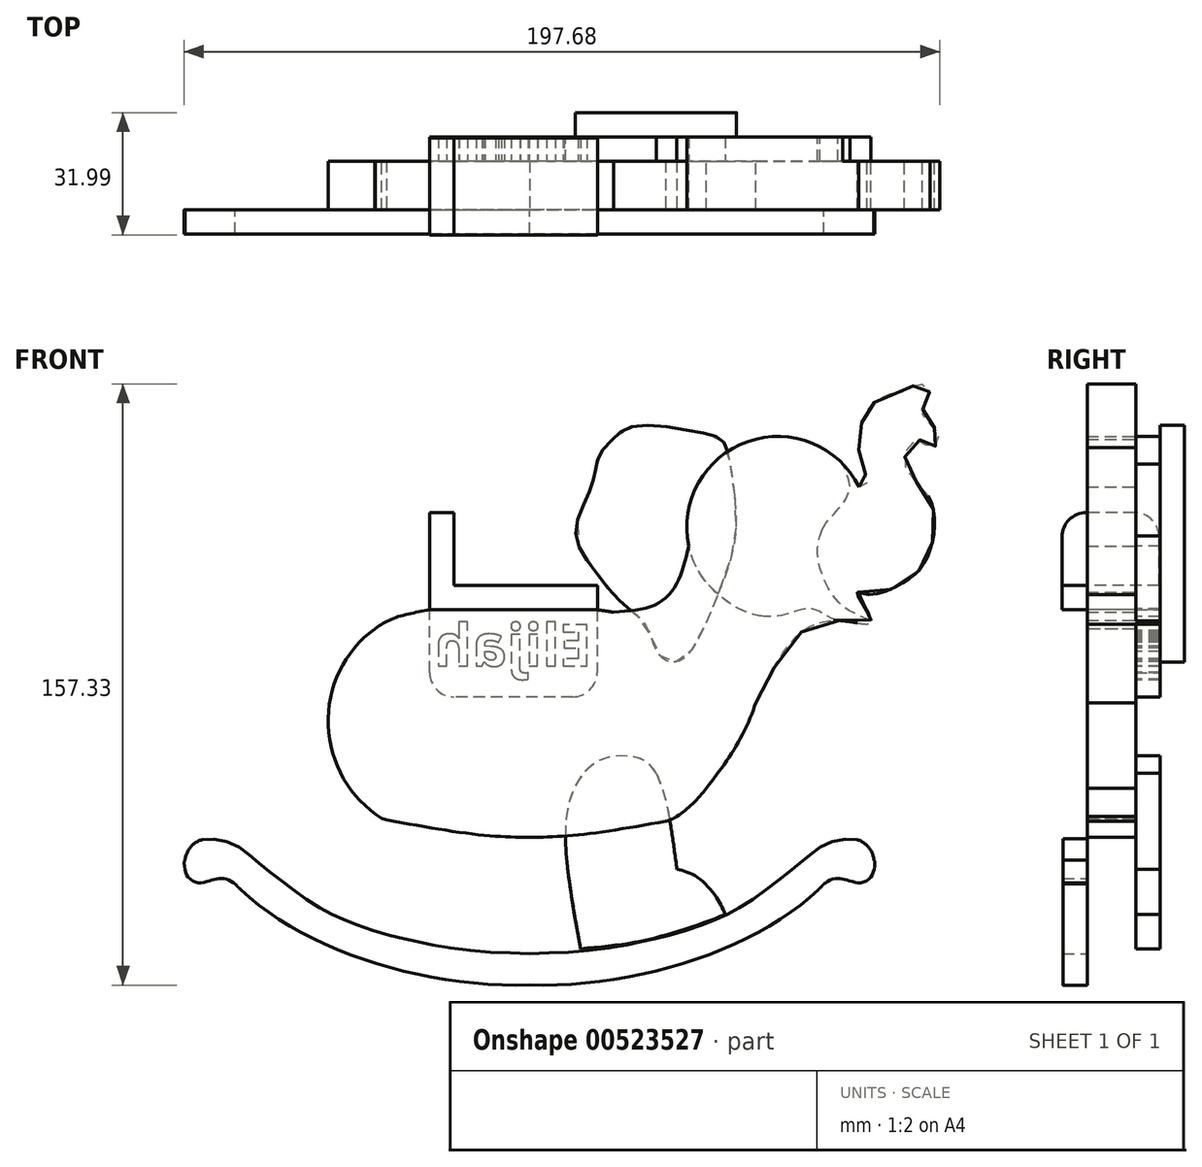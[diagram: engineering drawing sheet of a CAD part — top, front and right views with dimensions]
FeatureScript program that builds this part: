
annotation { "Feature Type Name" : "Feature", "Feature Type Description" : "" }
export const myFeature = defineFeature(function(context is Context, id is Id, definition is map)
    precondition{}
    {
        {
            var Q0;
            Q0=qCreatedBy(makeId("Front.planeOp"),FACE);
            var sketch = newSketch(context, id + "F0", { "sketchPlane" : qUnion([Q0])});
            skFitSpline(sketch, "E0", {"points": [v(-76.53, 25.4) * mm, v(0, 0) * mm, v(76.06, 25.4) * mm, v(96.85, 71.64) * mm], "startDerivative": vector(203.26, -102.2) * mm, "endDerivative": vector(39.96, 176.1) * mm});
            skLineSegment(sketch, "E1", {"start": v(0, 36.4) * mm, "end": v(0, -57.69) * mm});
            skFitSpline(sketch, "E2.MirrorCS", {"points": [v(76.53, 25.4) * mm, v(0, 0) * mm, v(-76.06, 25.4) * mm, v(-96.85, 71.64) * mm], "startDerivative": vector(-203.26, -102.2) * mm, "endDerivative": vector(-39.96, 176.1) * mm});
            skFitSpline(sketch, "E3", {"points": [v(-76.06, 25.4) * mm, v(-77.33, 26.6) * mm, v(-79.55, 27.71) * mm, v(-81.61, 27.71) * mm, v(-83.88, 27.19) * mm, v(-86.73, 26.71) * mm, v(-89.37, 28.3) * mm, v(-90.27, 30.99) * mm, v(-89.47, 33.26) * mm, v(-73.22, 31.4) * mm], "startDerivative": vector(-18.77, 20.22) * mm, "endDerivative": vector(33.5, -32.55) * mm});
            skFitSpline(sketch, "E4", {"points": [v(-90.27, 30.99) * mm, v(-89.65, 34.49) * mm, v(-86.83, 37.56) * mm, v(-82.56, 38.13) * mm, v(-77.29, 36.68) * mm, v(-73.14, 33.86) * mm, v(-68.87, 30.28) * mm, v(-63.67, 26.26) * mm, v(-57.14, 21.5) * mm, v(-51.36, 18.3) * mm, v(-46.78, 16.28) * mm, v(-37.87, 13.27) * mm, v(-31.25, 11.71) * mm, v(-24.13, 10.2) * mm, v(-12.07, 8.7) * mm, v(0, 8.2) * mm], "startDerivative": vector(3.66, 72.2) * mm, "endDerivative": vector(131.43, -3.03) * mm});
            skFitSpline(sketch, "E5.MirrorCS", {"points": [v(90.27, 30.99) * mm, v(89.65, 34.49) * mm, v(86.83, 37.56) * mm, v(82.56, 38.13) * mm, v(77.29, 36.68) * mm, v(73.14, 33.86) * mm, v(68.87, 30.28) * mm, v(63.67, 26.26) * mm, v(57.14, 21.5) * mm, v(51.36, 18.3) * mm, v(46.78, 16.28) * mm, v(37.87, 13.27) * mm, v(31.25, 11.71) * mm, v(24.13, 10.2) * mm, v(12.07, 8.7) * mm, v(0, 8.2) * mm], "startDerivative": vector(-3.66, 72.2) * mm, "endDerivative": vector(-131.43, -3.03) * mm});
            skFitSpline(sketch, "E6.MirrorCS", {"points": [v(76.06, 25.4) * mm, v(77.33, 26.6) * mm, v(79.55, 27.71) * mm, v(81.61, 27.71) * mm, v(83.88, 27.19) * mm, v(86.73, 26.71) * mm, v(89.37, 28.3) * mm, v(90.27, 30.99) * mm, v(89.47, 33.26) * mm, v(73.22, 31.4) * mm], "startDerivative": vector(18.77, 20.22) * mm, "endDerivative": vector(-33.5, -32.55) * mm});
            skSolve(sketch);
        }
        {
            var Q0;
            Q0 = qSketchRegion(id + "F0", true);
            extrude(context, id + "F1", {"entities" : qUnion([Q0]), "depth" : 6.35 * mm, "offsetDistance" : 25.4 * mm});
        }
        {
            var Q0;
            Q0=qCreatedBy(makeId("Front.planeOp"),FACE);
            var sketch = newSketch(context, id + "F2", { "sketchPlane" : qUnion([Q0])});
            skArc(sketch, "E7", {"start": v(38.56, 44.04) * mm, "mid": v(51.86, 69.38) * mm, "end": v(37.91, 94.37) * mm});
            skArc(sketch, "E8", {"start": v(-40.52, 93.16) * mm, "mid": v(-52.67, 67.9) * mm, "end": v(-38.68, 43.6) * mm});
            skFitSpline(sketch, "E9", {"points": [v(-38.11, 43.24) * mm, v(-12.9, 39.26) * mm, v(0, 38.6) * mm], "startDerivative": vector(46.68, -8.34) * mm, "endDerivative": vector(28.52, -0.51) * mm});
            skFitSpline(sketch, "E10.MirrorCS", {"points": [v(38.11, 43.24) * mm, v(12.9, 39.26) * mm, v(0, 38.6) * mm], "startDerivative": vector(-46.68, -8.34) * mm, "endDerivative": vector(-28.52, -0.51) * mm});
            skFitSpline(sketch, "E11.MirrorCS", {"points": [v(38.1, 94.76) * mm, v(12.9, 98.74) * mm, v(-0.01, 99.4) * mm], "startDerivative": vector(-46.68, 8.34) * mm, "endDerivative": vector(-28.52, 0.51) * mm});
            skFitSpline(sketch, "E12", {"points": [v(-40.52, 93.16) * mm, v(-38.55, 94.2) * mm, v(-35.5, 95.23) * mm], "startDerivative": vector(4.04, 2.4) * mm, "endDerivative": vector(5.93, 1.7) * mm});
            skFitSpline(sketch, "E13", {"points": [v(-38.68, 43.6) * mm, v(-37.48, 43.13) * mm], "startDerivative": vector(1.2, -0.46) * mm, "endDerivative": vector(1.2, -0.46) * mm});
            skFitSpline(sketch, "E14", {"points": [v(35.57, 42.79) * mm, v(37.13, 43.32) * mm, v(38.56, 44.04) * mm], "startDerivative": vector(3.17, 0.91) * mm, "endDerivative": vector(2.79, 1.63) * mm});
            skFitSpline(sketch, "E15", {"points": [v(37.91, 94.37) * mm, v(36.85, 94.86) * mm, v(35.85, 95.16) * mm], "startDerivative": vector(-2.04, 1.09) * mm, "endDerivative": vector(-2.08, 0.51) * mm});
            skLineSegment(sketch, "E16", {"start": v(-0.01, 99.4) * mm, "end": v(-0.17, 99.4) * mm});
            skLineSegment(sketch, "E17", {"start": v(17.65, 120.95) * mm, "end": v(17.65, 85.65) * mm});
            skLineSegment(sketch, "E18", {"start": v(-26.11, 120.16) * mm, "end": v(-26.11, 85.65) * mm});
            skLineSegment(sketch, "E19", {"start": v(17.65, 98.17) * mm, "end": v(-26.11, 98.17) * mm});
            skFitSpline(sketch, "E20", {"points": [v(-26.11, 98.17) * mm, v(-32.43, 96.87) * mm, v(-37.32, 95.15) * mm, v(-41.22, 92.63) * mm], "startDerivative": vector(-17.83, -3.3) * mm, "endDerivative": vector(-12.07, -8.87) * mm});
            skSolve(sketch);
        }
        {
            var Q0;
            Q0 = qSketchRegion(id + "F2", true);
            extrude(context, id + "F3", {"entities" : qUnion([Q0]), "oppositeDirection" : true, "depth" : 12.7 * mm, "offsetDistance" : 25.4 * mm});
        }
        {
            var Q0;
            Q0=makeQuery(id+"F3.opExtrude","CAP_FACE",FACE,{"disambiguationData":[OSD([sQuery(id+"F2.wireOp",EDGE,"E7"),sQuery(id+"F2.wireOp",EDGE,"E8"),sQuery(id+"F2.wireOp",EDGE,"E9"),sQuery(id+"F2.wireOp",EDGE,"E10.MirrorCS"),sQuery(id+"F2.wireOp",EDGE,"b9e27715-7742-40b8-b59a-87ce8d484c370.MirrorCS"),sQuery(id+"F2.wireOp",EDGE,"E11.MirrorCS"),sQuery(id+"F2.wireOp",EDGE,"E12"),sQuery(id+"F2.wireOp",EDGE,"E13"),sQuery(id+"F2.wireOp",EDGE,"E14"),sQuery(id+"F2.wireOp",EDGE,"E15"),sQuery(id+"F2.wireOp",EDGE,"E16")])],"isStart":false});
            var sketch = newSketch(context, id + "F4", { "sketchPlane" : qUnion([Q0])});
            skPoint(sketch, "E21.0.internal.snap0", {"position": v(-51.86, 69.38) * mm});
            skArc(sketch, "E22", {"start": v(-41.66, 114.78) * mm, "mid": v(-57.1, 142.17) * mm, "end": v(-86.2, 130.31) * mm});
            skFitSpline(sketch, "E23", {"points": [v(-46.24, 51.5) * mm, v(-53.71, 61.99) * mm, v(-59.22, 73.85) * mm, v(-61.63, 83.14) * mm, v(-66.1, 93.11) * mm, v(-69.59, 96.4) * mm], "startDerivative": vector(-34.32, 44.1) * mm, "endDerivative": vector(-25.28, 18.55) * mm});
            skFitSpline(sketch, "E24", {"points": [v(-41.66, 114.78) * mm, v(-38.56, 105.15) * mm, v(-32.9, 99.48) * mm, v(-22.03, 97.52) * mm], "startDerivative": vector(7.28, -30.1) * mm, "endDerivative": vector(33.32, -2.66) * mm});
            skFitSpline(sketch, "E25", {"points": [v(-59.22, 73.85) * mm, v(-64.03, 83.14) * mm, v(-72.21, 93.11) * mm, v(-83.03, 95.16) * mm, v(-89.35, 95.16) * mm, v(-85.7, 102.57) * mm, v(-88.57, 102.16) * mm, v(-97.37, 105.02) * mm, v(-102.27, 108.9) * mm, v(-105.14, 114.84) * mm, v(-105.95, 122.2) * mm, v(-103.82, 128.75) * mm, v(-99.29, 133.77) * mm, v(-98.23, 138.6) * mm, v(-100.73, 142.65) * mm, v(-103.05, 141.97) * mm, v(-104.6, 140.62) * mm, v(-106.72, 141.5) * mm, v(-107.1, 144.48) * mm, v(-104.79, 146.8) * mm, v(-102.76, 149.7) * mm, v(-103.82, 152.4) * mm, v(-104.79, 154.33) * mm, v(-103.82, 156.45) * mm, v(-101.5, 157.22) * mm, v(-98.7, 155.68) * mm, v(-97.07, 155) * mm, v(-94.46, 154.62) * mm, v(-90.8, 152.88) * mm, v(-88.38, 150.37) * mm, v(-86.74, 146.41) * mm, v(-86.16, 141.59) * mm, v(-86.74, 136.37) * mm, v(-88.1, 133.19) * mm, v(-88.1, 130.78) * mm, v(-86.2, 130.31) * mm], "startDerivative": vector(-96.74, 211.19) * mm, "endDerivative": vector(121.2, -2.17) * mm});
            skSolve(sketch);
        }
        {
            var Q0;
            Q0=makeQuery(id+"F4.imprint","IMPRINT",FACE,{"disambiguationData":[TD([[makeQuery(id+"F4.imprint","IMPRINT",EDGE,{"derivedFrom":sQuery(id+"F4.wireOp",EDGE,"E22")}),1.0]])]});
            extrude(context, id + "F5", {"entities" : qUnion([Q0]), "operationType" : NewBodyOperationType.ADD, "oppositeDirection" : true, "depth" : 12.7 * mm, "offsetDistance" : 25.4 * mm});
        }
        {
            var Q0;
            {var subQ0=sQuery(id+"F2.wireOp",EDGE,"E15");var subQ1=sQuery(id+"F2.wireOp",EDGE,"E11.MirrorCS");var subQ2=sQuery(id+"F2.wireOp",EDGE,"E7");Q0=makeQuery(id+"F5.boolean.opBoolean","MERGE",FACE,{"derivedFrom":[makeQuery(id+"F3.opExtrude","CAP_FACE",FACE,{"disambiguationData":[OSD([subQ2,sQuery(id+"F2.wireOp",EDGE,"E8"),sQuery(id+"F2.wireOp",EDGE,"E9"),sQuery(id+"F2.wireOp",EDGE,"E10.MirrorCS"),sQuery(id+"F2.wireOp",EDGE,"b9e27715-7742-40b8-b59a-87ce8d484c370.MirrorCS"),subQ1,sQuery(id+"F2.wireOp",EDGE,"E12"),sQuery(id+"F2.wireOp",EDGE,"E13"),sQuery(id+"F2.wireOp",EDGE,"E14"),subQ0,sQuery(id+"F2.wireOp",EDGE,"E16")])],"isStart":false}),makeQuery(id+"F5.opExtrude","CAP_FACE",FACE,{"disambiguationData":[OSD([subQ2,subQ1,subQ0,sQuery(id+"F4.wireOp",EDGE,"E22"),sQuery(id+"F4.wireOp",EDGE,"E23"),sQuery(id+"F4.wireOp",EDGE,"E24"),sQuery(id+"F4.wireOp",EDGE,"E25")])],"isStart":true})]});}
            var sketch = newSketch(context, id + "F6", { "sketchPlane" : qUnion([Q0])});
            skFitSpline(sketch, "E26", {"points": [v(-85.99, 102.76) * mm, v(-81.96, 101.28) * mm, v(-76.64, 111.46) * mm, v(-76.5, 119.05) * mm, v(-81.01, 124.73) * mm, v(-83.2, 128.08) * mm, v(-83.78, 130.85) * mm, v(-81.95, 136.3) * mm], "startDerivative": vector(25.96, 18.55) * mm, "endDerivative": vector(17.76, 40.73) * mm});
            skFitSpline(sketch, "E27", {"points": [v(-81.96, 95.29) * mm, v(-74.16, 98.34) * mm, v(-66.87, 96.89) * mm, v(-57.25, 97.32) * mm, v(-47.33, 104.18) * mm, v(-43.1, 110.44) * mm, v(-41.66, 114.78) * mm], "startDerivative": vector(49.84, -4.86) * mm, "endDerivative": vector(9.24, 33.73) * mm});
            skFitSpline(sketch, "E28", {"points": [v(-89.36, 95.22) * mm, v(-82.42, 98.8) * mm, v(-78.05, 104.05) * mm, v(-75.32, 113) * mm, v(-76.5, 119.05) * mm], "startDerivative": vector(29.34, 12.58) * mm, "endDerivative": vector(-8.34, 24.8) * mm});
            skFitSpline(sketch, "E29", {"points": [v(-80.65, 95.36) * mm, v(-69.61, 95.62) * mm, v(-61.21, 96.43) * mm], "startDerivative": vector(21.4, 0.15) * mm, "endDerivative": vector(17.38, 2.04) * mm});
            skSolve(sketch);
        }
        {
            var Q0;
            {var subQ6=sQuery(id+"F6.wireOp",EDGE,"E26");Q0=makeQuery(id+"F6.imprint","IMPRINT",FACE,{"disambiguationData":[TD([[makeQuery(id+"F6.imprint","IMPRINT",EDGE,{"derivedFrom":subQ6}),-1.0]])]});}
            extrude(context, id + "F7", {"entities" : qUnion([Q0]), "operationType" : NewBodyOperationType.ADD, "depth" : 6.35 * mm, "offsetDistance" : 25.4 * mm});
        }
        {
            var Q0;
            Q0=makeQuery(id+"F7.opExtrude","CAP_FACE",FACE,{"disambiguationData":[OSD([sQuery(id+"F4.wireOp",EDGE,"E22"),sQuery(id+"F4.wireOp",EDGE,"E25"),sQuery(id+"F6.wireOp",EDGE,"E26"),sQuery(id+"F6.wireOp",EDGE,"E27")])],"isStart":false});
            var sketch = newSketch(context, id + "F8", { "sketchPlane" : qUnion([Q0])});
            skPoint(sketch, "E30.22.internal.snap0", {"position": v(-53.71, 140.7) * mm});
            skFitSpline(sketch, "E31", {"points": [v(-53.71, 128.26) * mm, v(-51.86, 139.6) * mm, v(-49.82, 142.9) * mm, v(-41.96, 145.08) * mm, v(-27.32, 146.17) * mm, v(-21.86, 142.9) * mm, v(-17.93, 137.87) * mm, v(-17.06, 133.5) * mm, v(-14.87, 127.38) * mm, v(-12.03, 118.21) * mm, v(-15.96, 109.9) * mm, v(-24.05, 100.08) * mm, v(-30.38, 94.18) * mm, v(-33, 87.85) * mm, v(-36.06, 84.79) * mm, v(-39.56, 85) * mm, v(-43.7, 89.6) * mm, v(-49.36, 102.2) * mm, v(-53.71, 115.8) * mm, v(-53.71, 128.26) * mm]});
            skSolve(sketch);
        }
        {
            var Q0;
            {var subQ0=sQuery(id+"F8.wireOp",EDGE,"E31");var subQ1=makeQuery(id+"F7.opExtrude","CAP_EDGE",EDGE,{"disambiguationData":[OSD([sQuery(id+"F6.wireOp",EDGE,"E27")])],"isStart":false});var subQ2=makeQuery(id+"F8.imprint","INTERSECT",VERTEX,{"derivedFrom":[subQ1,subQ0]});Q0=makeQuery(id+"F8.imprint","IMPRINT",FACE,{"disambiguationData":[TD([[makeQuery(id+"F8.imprint","IMPRINT",EDGE,{"disambiguationData":[TD([[subQ2,1.0]])],"derivedFrom":subQ0}),-1.0]])]});}
            var Q1;
            {var subQ0=sQuery(id+"F8.wireOp",EDGE,"E31");var subQ1=makeQuery(id+"F7.opExtrude","CAP_EDGE",EDGE,{"disambiguationData":[OSD([sQuery(id+"F6.wireOp",EDGE,"E27")])],"isStart":false});var subQ2=makeQuery(id+"F8.imprint","INTERSECT",VERTEX,{"derivedFrom":[subQ1,subQ0]});Q1=makeQuery(id+"F8.imprint","IMPRINT",FACE,{"disambiguationData":[TD([[makeQuery(id+"F8.imprint","IMPRINT",EDGE,{"disambiguationData":[TD([[subQ2,-1.0]])],"derivedFrom":subQ0}),-1.0]])]});}
            extrude(context, id + "F9", {"entities" : qUnion([Q0, Q1]), "operationType" : NewBodyOperationType.ADD, "depth" : 6.35 * mm, "offsetDistance" : 25.4 * mm});
        }
        {
            var Q0;
            {var subQ0=sQuery(id+"F2.wireOp",EDGE,"E16");var subQ1=sQuery(id+"F2.wireOp",EDGE,"E14");var subQ2=sQuery(id+"F2.wireOp",EDGE,"E13");var subQ3=sQuery(id+"F4.wireOp",EDGE,"E25");var subQ4=sQuery(id+"F2.wireOp",EDGE,"E12");var subQ5=sQuery(id+"F4.wireOp",EDGE,"E24");var subQ6=sQuery(id+"F2.wireOp",EDGE,"E11.MirrorCS");var subQ7=sQuery(id+"F4.wireOp",EDGE,"E23");var subQ8=sQuery(id+"F2.wireOp",EDGE,"b9e27715-7742-40b8-b59a-87ce8d484c370.MirrorCS");var subQ9=sQuery(id+"F2.wireOp",EDGE,"E7");var subQ10=sQuery(id+"F2.wireOp",EDGE,"E10.MirrorCS");var subQ11=sQuery(id+"F2.wireOp",EDGE,"E8");var subQ12=sQuery(id+"F2.wireOp",EDGE,"E9");var subQ13=sQuery(id+"F4.wireOp",EDGE,"E22");var subQ15=sQuery(id+"F2.wireOp",EDGE,"E15");Q0=makeQuery(id+"F7.boolean.opBoolean","SPLIT",FACE,{"disambiguationData":[TD([makeQuery(id+"F3.opExtrude","SWEPT_FACE",FACE,{"disambiguationData":[OSD([subQ9])]})])],"derivedFrom":makeQuery(id+"F5.boolean.opBoolean","MERGE",FACE,{"derivedFrom":[makeQuery(id+"F3.opExtrude","CAP_FACE",FACE,{"disambiguationData":[OSD([subQ9,subQ11,subQ12,subQ10,subQ8,subQ6,subQ4,subQ2,subQ1,subQ15,subQ0])],"isStart":false}),makeQuery(id+"F5.opExtrude","CAP_FACE",FACE,{"disambiguationData":[OSD([subQ9,subQ6,subQ15,subQ13,subQ7,subQ5,subQ3])],"isStart":true})]})});}
            var sketch = newSketch(context, id + "F10", { "sketchPlane" : qUnion([Q0])});
            skFitSpline(sketch, "E32", {"points": [v(-33.13, 55.4) * mm, v(-30.36, 58.52) * mm, v(-24.29, 59.9) * mm, v(-17, 58) * mm, v(-10.94, 49.68) * mm, v(-9.55, 34.76) * mm, v(-13.36, 9.45) * mm], "startDerivative": vector(21.71, 33.22) * mm, "endDerivative": vector(-18.9, -102.55) * mm});
            skFitSpline(sketch, "E33", {"points": [v(-13.36, 9.45) * mm, v(-27.75, 11.19) * mm, v(-40.41, 14.48) * mm, v(-51.16, 18.47) * mm, v(-56.7, 21.42) * mm], "startDerivative": vector(-51.3, 4.67) * mm, "endDerivative": vector(-26.74, 15.53) * mm});
            skFitSpline(sketch, "E34", {"points": [v(-33.13, 55.4) * mm, v(-35.57, 48.46) * mm, v(-38.56, 30.26) * mm], "startDerivative": vector(-6.57, -15.64) * mm, "endDerivative": vector(-4.45, -33.3) * mm});
            skFitSpline(sketch, "E35", {"points": [v(-38.56, 30.26) * mm, v(-43.36, 28.52) * mm, v(-48.9, 22.98) * mm, v(-51.16, 18.47) * mm], "startDerivative": vector(-15.3, -3.48) * mm, "endDerivative": vector(-5.69, -14.13) * mm});
            skSolve(sketch);
        }
        {
            var Q0;
            {var subQ4=sQuery(id+"F10.wireOp",EDGE,"E33");Q0=makeQuery(id+"F10.imprint","IMPRINT",FACE,{"disambiguationData":[TD([[makeQuery(id+"F10.imprint","IMPRINT",EDGE,{"derivedFrom":subQ4}),-1.0]])]});}
            var Q1;
            {var subQ0=sQuery(id+"F10.wireOp",EDGE,"E34");var subQ1=sQuery(id+"F10.wireOp",EDGE,"E32");var subQ2=makeQuery(id+"F10.imprint","INTERSECT",VERTEX,{"derivedFrom":[subQ1,subQ0]});Q1=makeQuery(id+"F10.imprint","IMPRINT",FACE,{"disambiguationData":[TD([[makeQuery(id+"F10.imprint","IMPRINT",EDGE,{"disambiguationData":[TD([[subQ2,-1.0]])],"derivedFrom":subQ1}),-1.0]])]});}
            extrude(context, id + "F11", {"entities" : qUnion([Q0, Q1]), "operationType" : NewBodyOperationType.ADD, "depth" : 6.35 * mm, "offsetDistance" : 25.4 * mm});
        }
        {
            var Q0;
            {var subQ0=sQuery(id+"F2.wireOp",EDGE,"E16");var subQ1=sQuery(id+"F2.wireOp",EDGE,"E14");var subQ2=sQuery(id+"F2.wireOp",EDGE,"E13");var subQ3=sQuery(id+"F4.wireOp",EDGE,"E25");var subQ4=sQuery(id+"F2.wireOp",EDGE,"E12");var subQ5=sQuery(id+"F4.wireOp",EDGE,"E24");var subQ6=sQuery(id+"F2.wireOp",EDGE,"E11.MirrorCS");var subQ7=sQuery(id+"F4.wireOp",EDGE,"E23");var subQ8=sQuery(id+"F2.wireOp",EDGE,"b9e27715-7742-40b8-b59a-87ce8d484c370.MirrorCS");var subQ9=sQuery(id+"F2.wireOp",EDGE,"E7");var subQ10=sQuery(id+"F2.wireOp",EDGE,"E10.MirrorCS");var subQ11=sQuery(id+"F2.wireOp",EDGE,"E8");var subQ12=sQuery(id+"F2.wireOp",EDGE,"E9");var subQ13=sQuery(id+"F4.wireOp",EDGE,"E22");var subQ15=sQuery(id+"F2.wireOp",EDGE,"E15");Q0=makeQuery(id+"F7.boolean.opBoolean","SPLIT",FACE,{"disambiguationData":[TD([makeQuery(id+"F3.opExtrude","SWEPT_FACE",FACE,{"disambiguationData":[OSD([subQ9])]})])],"derivedFrom":makeQuery(id+"F5.boolean.opBoolean","MERGE",FACE,{"derivedFrom":[makeQuery(id+"F3.opExtrude","CAP_FACE",FACE,{"disambiguationData":[OSD([subQ9,subQ11,subQ12,subQ10,subQ8,subQ6,subQ4,subQ2,subQ1,subQ15,subQ0])],"isStart":false}),makeQuery(id+"F5.opExtrude","CAP_FACE",FACE,{"disambiguationData":[OSD([subQ9,subQ6,subQ15,subQ13,subQ7,subQ5,subQ3])],"isStart":true})]})});}
            var sketch = newSketch(context, id + "F12", { "sketchPlane" : qUnion([Q0])});
            skLineSegment(sketch, "E36", {"start": v(-11.31, 75.37) * mm, "end": v(19.77, 75.37) * mm});
            skText(sketch, "E37", { "text": "Elijah", "fontName": "OpenSans-Bold.ttf"});
            skLineSegment(sketch, "E38", {"start": v(-17.66, 98.16) * mm, "end": v(-17.66, 81.72) * mm});
            skLineSegment(sketch, "E39", {"start": v(-17.66, 75.37) * mm, "end": v(-17.66, 75.37) * mm});
            skLineSegment(sketch, "E40", {"start": v(24.23, 75.37) * mm, "end": v(26.12, 75.37) * mm});
            skLineSegment(sketch, "E41", {"start": v(26.12, 81.72) * mm, "end": v(26.12, 96.86) * mm});
            skLineSegment(sketch, "E42", {"start": v(-17.66, 98.16) * mm, "end": v(26.12, 98.16) * mm});
            skLineSegment(sketch, "E43", {"start": v(26.12, 98.16) * mm, "end": v(26.12, 96.86) * mm});
            skPoint(sketch, "E44.visualSharp", {"position": v(-17.66, 75.37) * mm});
            skArc(sketch, "E44.filletArc", {"start": v(-17.66, 81.72) * mm, "mid": v(-15.8, 77.23) * mm, "end": v(-11.31, 75.37) * mm});
            skPoint(sketch, "E45.newPointB", {"position": v(26.12, 75.37) * mm});
            skArc(sketch, "E45.filletArc", {"start": v(19.77, 75.37) * mm, "mid": v(24.26, 77.23) * mm, "end": v(26.12, 81.72) * mm});
            const initialGuessF12  = {"E37": [-0.0164, 0.08346, 1, 0, 0.0109]};
            skSetInitialGuess(sketch, initialGuessF12);
            skSolve(sketch);
        }
        {
            var Q0;
            Q0=makeQuery(id+"F12.imprint","IMPRINT",FACE,{"disambiguationData":[TD([[makeQuery(id+"F12.imprint","IMPRINT",EDGE,{"derivedFrom":sQuery(id+"F12.wireOp",EDGE,"E36")}),1.0]])]});
            var Q1;
            Q1=makeQuery(id+"F12.imprint","IMPRINT",FACE,{"disambiguationData":[TD([[makeQuery(id+"F12.imprint","IMPRINT",EDGE,{"derivedFrom":sQuery(id+"F12.wireOp",EDGE,"E37.sketch_text.stroke-58")}),1.0]])]});
            extrude(context, id + "F13", {"entities" : qUnion([Q0, Q1]), "operationType" : NewBodyOperationType.ADD, "depth" : 6.35 * mm, "offsetDistance" : 25.4 * mm});
        }
        {
            var Q0;
            Q0=makeQuery(id+"F3.opExtrude","SWEPT_FACE",FACE,{"disambiguationData":[OSD([sQuery(id+"F2.wireOp",EDGE,"E19")])]});
            var sketch = newSketch(context, id + "F14", { "sketchPlane" : qUnion([Q0])});
            skLineSegment(sketch, "E46.bottom", {"start": v(17.79, 18.8) * mm, "end": v(-26.1, 18.8) * mm});
            skLineSegment(sketch, "E46.top", {"start": v(17.79, -6.6) * mm, "end": v(-26.1, -6.6) * mm});
            skLineSegment(sketch, "E46.left", {"start": v(17.79, 18.8) * mm, "end": v(17.79, -6.6) * mm});
            skLineSegment(sketch, "E46.right", {"start": v(-26.1, 18.8) * mm, "end": v(-26.1, -6.6) * mm});
            skSolve(sketch);
        }
        {
            var Q0;
            {var subQ1=sQuery(id+"F14.wireOp",EDGE,"E46.bottom");Q0=makeQuery(id+"F14.imprint","IMPRINT",FACE,{"disambiguationData":[TD([[makeQuery(id+"F14.imprint","IMPRINT",EDGE,{"derivedFrom":subQ1}),1.0]])]});}
            var Q1;
            {var subQ1=sQuery(id+"F2.wireOp",EDGE,"E19");var subQ6=makeQuery(id+"F3.opExtrude","SWEPT_EDGE",EDGE,{"disambiguationData":[OSD([sQuery(id+"F2.wireOp",EDGE,"E17"),subQ1])]});Q1=makeQuery(id+"F14.imprint","IMPRINT",FACE,{"disambiguationData":[TD([[makeQuery(id+"F14.imprint","IMPRINT",EDGE,{"derivedFrom":subQ6}),-1.0]])]});}
            extrude(context, id + "F15", {"entities" : qUnion([Q0, Q1]), "operationType" : NewBodyOperationType.ADD, "depth" : 6.35 * mm, "offsetDistance" : 25.4 * mm});
        }
        {
            var Q0;
            Q0=makeQuery(id+"F15.opExtrude","SWEPT_FACE",FACE,{"disambiguationData":[OSD([sQuery(id+"F14.wireOp",EDGE,"E46.right")])]});
            var sketch = newSketch(context, id + "F16", { "sketchPlane" : qUnion([Q0])});
            skLineSegment(sketch, "E47.bottom", {"start": v(-18.8, 104.52) * mm, "end": v(6.6, 104.52) * mm});
            skLineSegment(sketch, "E47.top", {"start": v(-12.46, 123.57) * mm, "end": v(0.24, 123.57) * mm});
            skLineSegment(sketch, "E47.left", {"start": v(-18.8, 104.52) * mm, "end": v(-18.8, 117.22) * mm});
            skLineSegment(sketch, "E47.right", {"start": v(6.6, 104.52) * mm, "end": v(6.6, 117.22) * mm});
            skPoint(sketch, "E48.visualSharp", {"position": v(-18.8, 123.57) * mm});
            skArc(sketch, "E48.filletArc", {"start": v(-12.46, 123.57) * mm, "mid": v(-16.95, 121.71) * mm, "end": v(-18.8, 117.22) * mm});
            skPoint(sketch, "E49.visualSharp", {"position": v(6.6, 123.57) * mm});
            skArc(sketch, "E49.filletArc", {"start": v(6.6, 117.22) * mm, "mid": v(4.73, 121.71) * mm, "end": v(0.24, 123.57) * mm});
            skSolve(sketch);
        }
        {
            var Q0;
            Q0=makeQuery(id+"F16.imprint","IMPRINT",FACE,{"disambiguationData":[TD([[makeQuery(id+"F16.imprint","IMPRINT",EDGE,{"derivedFrom":sQuery(id+"F16.wireOp",EDGE,"E47.bottom")}),1.0]])]});
            extrude(context, id + "F17", {"entities" : qUnion([Q0]), "operationType" : NewBodyOperationType.ADD, "oppositeDirection" : true, "depth" : 6.35 * mm, "offsetDistance" : 25.4 * mm});
        }
    });
